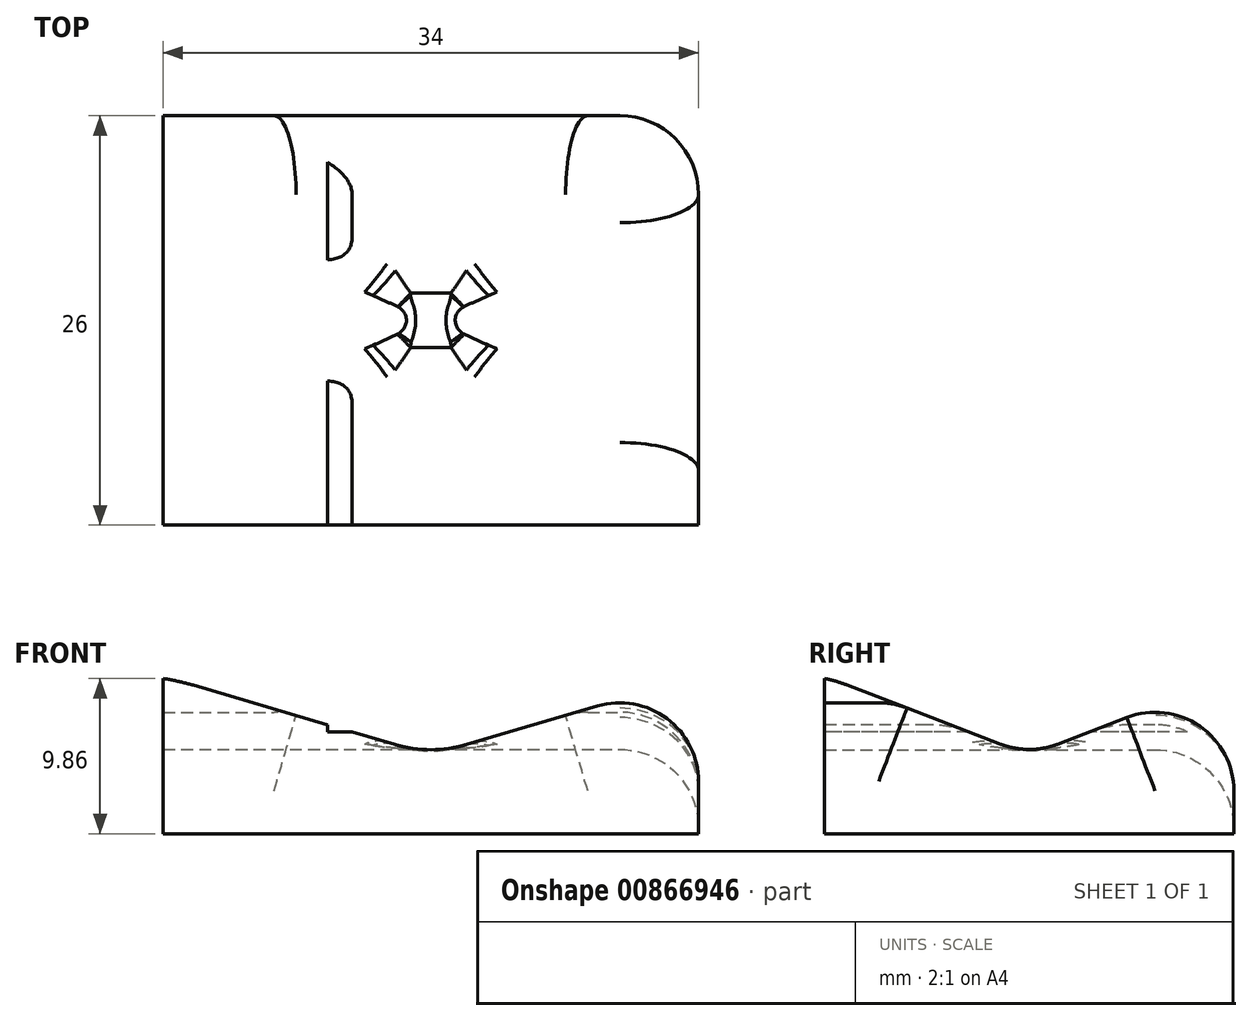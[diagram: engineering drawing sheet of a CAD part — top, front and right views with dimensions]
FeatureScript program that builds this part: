
annotation { "Feature Type Name" : "Feature", "Feature Type Description" : "" }
export const myFeature = defineFeature(function(context is Context, id is Id, definition is map)
    precondition{}
    {
        {
            var Q0;
            Q0=qCreatedBy(makeId("Top.planeOp"),FACE);
            var sketch = newSketch(context, id + "F0", { "sketchPlane" : qUnion([Q0])});
            skLineSegment(sketch, "E0.bottom", {"start": v(-17, -13) * mm, "end": v(17, -13) * mm});
            skLineSegment(sketch, "E0.top", {"start": v(-17, 13) * mm, "end": v(17, 13) * mm});
            skLineSegment(sketch, "E0.left", {"start": v(-17, -13) * mm, "end": v(-17, 13) * mm});
            skLineSegment(sketch, "E0.right", {"start": v(17, -13) * mm, "end": v(17, 13) * mm});
            skLineSegment(sketch, "E1", {"start": v(-17, 13) * mm, "end": v(17, -13) * mm, "construction": true});
            skSolve(sketch);
        }
        {
            var Q0;
            Q0 = qSketchRegion(id + "F0", true);
            extrude(context, id + "F1", {"entities" : qUnion([Q0]), "depth" : 10 * mm, "offsetDistance" : 25 * mm});
        }
        {
            var Q0;
            Q0=makeQuery(id+"F1.opExtrude","SWEPT_FACE",FACE,{"disambiguationData":[OSD([sQuery(id+"F0.wireOp",EDGE,"E0.left")])]});
            var sketch = newSketch(context, id + "F2", { "sketchPlane" : qUnion([Q0])});
            skLineSegment(sketch, "E2", {"start": v(-13, 10) * mm, "end": v(0, 5) * mm});
            skLineSegment(sketch, "E3", {"start": v(0, 5) * mm, "end": v(13, 10) * mm});
            skLineSegment(sketch, "E4", {"start": v(-13, 10) * mm, "end": v(13, 10) * mm});
            skSolve(sketch);
        }
        {
            var Q0;
            Q0 = qSketchRegion(id + "F2", true);
            extrude(context, id + "F3", {"entities" : qUnion([Q0]), "operationType" : NewBodyOperationType.REMOVE, "endBound" : BoundingType.THROUGH_ALL, "oppositeDirection" : true, "depth" : 25 * mm, "offsetDistance" : 25 * mm});
        }
        {
            var Q0;
            Q0=makeQuery(id+"F1.opExtrude","SWEPT_FACE",FACE,{"disambiguationData":[OSD([sQuery(id+"F0.wireOp",EDGE,"E0.bottom")])]});
            var sketch = newSketch(context, id + "F4", { "sketchPlane" : qUnion([Q0])});
            skLineSegment(sketch, "E5", {"start": v(-17, 10) * mm, "end": v(0, 5) * mm});
            skLineSegment(sketch, "E6", {"start": v(0, 5) * mm, "end": v(17, 10) * mm});
            skLineSegment(sketch, "E7", {"start": v(17, 10) * mm, "end": v(-17, 10) * mm});
            skSolve(sketch);
        }
        {
            var Q0;
            Q0 = qSketchRegion(id + "F4", true);
            extrude(context, id + "F5", {"entities" : qUnion([Q0]), "operationType" : NewBodyOperationType.REMOVE, "endBound" : BoundingType.THROUGH_ALL, "oppositeDirection" : true, "depth" : 25 * mm, "offsetDistance" : 25 * mm});
        }
        {
            var Q0;
            {var subQ0=sQuery(id+"F2.wireOp",EDGE,"E3");var subQ1=sQuery(id+"F2.wireOp",EDGE,"E2");Q0=makeQuery(id+"F5.boolean.opBoolean","SPLIT",EDGE,{"disambiguationData":[TD([makeQuery(id+"F1.opExtrude","SWEPT_FACE",FACE,{"disambiguationData":[OSD([sQuery(id+"F0.wireOp",EDGE,"E0.left")])]})])],"derivedFrom":makeQuery(id+"F3.boolean.opBoolean","COPY",EDGE,{"derivedFrom":makeQuery(id+"F3.opExtrude","SWEPT_EDGE",EDGE,{"disambiguationData":[OSD([subQ1,subQ0])]})})});}
            var Q1;
            {var subQ0=sQuery(id+"F2.wireOp",EDGE,"E3");var subQ1=sQuery(id+"F2.wireOp",EDGE,"E2");Q1=makeQuery(id+"F5.boolean.opBoolean","SPLIT",EDGE,{"disambiguationData":[TD([makeQuery(id+"F1.opExtrude","SWEPT_FACE",FACE,{"disambiguationData":[OSD([sQuery(id+"F0.wireOp",EDGE,"E0.right")])]})])],"derivedFrom":makeQuery(id+"F3.boolean.opBoolean","COPY",EDGE,{"derivedFrom":makeQuery(id+"F3.opExtrude","SWEPT_EDGE",EDGE,{"disambiguationData":[OSD([subQ1,subQ0])]})})});}
            fillet(context, id + "F6", {"entities" : qUnion([Q0, Q1]), "radius" : 5 * mm, "tangentPropagation" : true, "allowEdgeOverflow" : false});
        }
        {
            var Q0;
            {var subQ0=sQuery(id+"F4.wireOp",EDGE,"E5");var subQ1=sQuery(id+"F4.wireOp",EDGE,"E6");Q0=makeQuery(id+"F5.boolean.opBoolean","COPY",EDGE,{"disambiguationData":[TD([makeQuery(id+"F1.opExtrude","SWEPT_FACE",FACE,{"disambiguationData":[OSD([sQuery(id+"F0.wireOp",EDGE,"E0.top")])]})])],"derivedFrom":makeQuery(id+"F5.opExtrude","SWEPT_EDGE",EDGE,{"disambiguationData":[OSD([subQ0,subQ1])]})});}
            fillet(context, id + "F7", {"entities" : qUnion([Q0]), "radius" : 8 * mm, "tangentPropagation" : true, "allowEdgeOverflow" : false});
        }
        {
            var Q0;
            Q0=makeQuery(id+"F5.boolean.opBoolean","INTERSECT",EDGE,{"derivedFrom":[makeQuery(id+"F1.opExtrude","SWEPT_FACE",FACE,{"disambiguationData":[OSD([sQuery(id+"F0.wireOp",EDGE,"E0.top")])]}),makeQuery(id+"F5.opExtrude","SWEPT_FACE",FACE,{"disambiguationData":[OSD([sQuery(id+"F4.wireOp",EDGE,"E5")])]})]});
            var Q1;
            {var subQ0=makeQuery(id+"F1.opExtrude","SWEPT_FACE",FACE,{"disambiguationData":[OSD([sQuery(id+"F0.wireOp",EDGE,"E0.top")])]});var subQ1=sQuery(id+"F4.wireOp",EDGE,"E5");var subQ2=sQuery(id+"F4.wireOp",EDGE,"E6");Q1=makeQuery(id+"F7.opFillet","BLEND_EDGE",EDGE,{"blendedFrom":[makeQuery(id+"F5.boolean.opBoolean","COPY",EDGE,{"disambiguationData":[TD([subQ0])],"derivedFrom":makeQuery(id+"F5.opExtrude","SWEPT_EDGE",EDGE,{"disambiguationData":[OSD([subQ1,subQ2])]})}),subQ0],"blendedInto":[subQ0]});}
            var Q2;
            Q2=makeQuery(id+"F5.boolean.opBoolean","INTERSECT",EDGE,{"derivedFrom":[makeQuery(id+"F1.opExtrude","SWEPT_FACE",FACE,{"disambiguationData":[OSD([sQuery(id+"F0.wireOp",EDGE,"E0.top")])]}),makeQuery(id+"F5.opExtrude","SWEPT_FACE",FACE,{"disambiguationData":[OSD([sQuery(id+"F4.wireOp",EDGE,"E6")])]})]});
            var Q3;
            Q3=makeQuery(id+"F3.boolean.opBoolean","INTERSECT",EDGE,{"derivedFrom":[makeQuery(id+"F1.opExtrude","SWEPT_FACE",FACE,{"disambiguationData":[OSD([sQuery(id+"F0.wireOp",EDGE,"E0.right")])]}),makeQuery(id+"F3.opExtrude","SWEPT_FACE",FACE,{"disambiguationData":[OSD([sQuery(id+"F2.wireOp",EDGE,"E2")])]})]});
            var Q4;
            Q4=makeQuery(id+"F3.boolean.opBoolean","COPY",EDGE,{"derivedFrom":makeQuery(id+"F3.opExtrude","CAP_EDGE",EDGE,{"disambiguationData":[OSD([sQuery(id+"F2.wireOp",EDGE,"E2")])],"isStart":true})});
            var Q5;
            Q5=makeQuery(id+"F5.boolean.opBoolean","COPY",EDGE,{"derivedFrom":makeQuery(id+"F5.opExtrude","CAP_EDGE",EDGE,{"disambiguationData":[OSD([sQuery(id+"F4.wireOp",EDGE,"E5")])],"isStart":true})});
            var Q6;
            Q6=makeQuery(id+"F5.boolean.opBoolean","COPY",EDGE,{"derivedFrom":makeQuery(id+"F5.opExtrude","CAP_EDGE",EDGE,{"disambiguationData":[OSD([sQuery(id+"F4.wireOp",EDGE,"E6")])],"isStart":true})});
            fillet(context, id + "F8", {"entities" : qUnion([Q0, Q1, Q2, Q3, Q4, Q5, Q6]), "radius" : 5 * mm, "tangentPropagation" : true, "allowEdgeOverflow" : false});
        }
        {
            var Q0;
            Q0=makeQuery(id+"F5.boolean.opBoolean","INTERSECT",EDGE,{"derivedFrom":[makeQuery(id+"F3.boolean.opBoolean","COPY",FACE,{"derivedFrom":makeQuery(id+"F3.opExtrude","SWEPT_FACE",FACE,{"disambiguationData":[OSD([sQuery(id+"F2.wireOp",EDGE,"E2")])]})}),makeQuery(id+"F5.opExtrude","SWEPT_FACE",FACE,{"disambiguationData":[OSD([sQuery(id+"F4.wireOp",EDGE,"E5")])]})]});
            var Q1;
            Q1=makeQuery(id+"F5.boolean.opBoolean","INTERSECT",EDGE,{"derivedFrom":[makeQuery(id+"F3.boolean.opBoolean","COPY",FACE,{"derivedFrom":makeQuery(id+"F3.opExtrude","SWEPT_FACE",FACE,{"disambiguationData":[OSD([sQuery(id+"F2.wireOp",EDGE,"E3")])]})}),makeQuery(id+"F5.opExtrude","SWEPT_FACE",FACE,{"disambiguationData":[OSD([sQuery(id+"F4.wireOp",EDGE,"E5")])]})]});
            var Q2;
            Q2=makeQuery(id+"F8.opFillet","BLEND_EDGE",EDGE,{"blendedFrom":[makeQuery(id+"F3.boolean.opBoolean","COPY",EDGE,{"derivedFrom":makeQuery(id+"F3.opExtrude","CAP_EDGE",EDGE,{"disambiguationData":[OSD([sQuery(id+"F2.wireOp",EDGE,"E3")])],"isStart":true})}),makeQuery(id+"F5.boolean.opBoolean","COPY",EDGE,{"derivedFrom":makeQuery(id+"F5.opExtrude","CAP_EDGE",EDGE,{"disambiguationData":[OSD([sQuery(id+"F4.wireOp",EDGE,"E5")])],"isStart":true})})],"blendedInto":[]});
            var Q3;
            Q3=makeQuery(id+"F8.opFillet","BLEND_EDGE",EDGE,{"blendedFrom":[makeQuery(id+"F3.boolean.opBoolean","INTERSECT",EDGE,{"derivedFrom":[makeQuery(id+"F1.opExtrude","SWEPT_FACE",FACE,{"disambiguationData":[OSD([sQuery(id+"F0.wireOp",EDGE,"E0.right")])]}),makeQuery(id+"F3.opExtrude","SWEPT_FACE",FACE,{"disambiguationData":[OSD([sQuery(id+"F2.wireOp",EDGE,"E3")])]})]}),makeQuery(id+"F5.boolean.opBoolean","COPY",EDGE,{"derivedFrom":makeQuery(id+"F5.opExtrude","CAP_EDGE",EDGE,{"disambiguationData":[OSD([sQuery(id+"F4.wireOp",EDGE,"E6")])],"isStart":true})})],"blendedInto":[]});
            var Q4;
            Q4=makeQuery(id+"F8.opFillet","BLEND_EDGE",EDGE,{"blendedFrom":[makeQuery(id+"F3.boolean.opBoolean","INTERSECT",EDGE,{"derivedFrom":[makeQuery(id+"F1.opExtrude","SWEPT_FACE",FACE,{"disambiguationData":[OSD([sQuery(id+"F0.wireOp",EDGE,"E0.right")])]}),makeQuery(id+"F3.opExtrude","SWEPT_FACE",FACE,{"disambiguationData":[OSD([sQuery(id+"F2.wireOp",EDGE,"E2")])]})]}),makeQuery(id+"F5.boolean.opBoolean","INTERSECT",EDGE,{"derivedFrom":[makeQuery(id+"F1.opExtrude","SWEPT_FACE",FACE,{"disambiguationData":[OSD([sQuery(id+"F0.wireOp",EDGE,"E0.top")])]}),makeQuery(id+"F5.opExtrude","SWEPT_FACE",FACE,{"disambiguationData":[OSD([sQuery(id+"F4.wireOp",EDGE,"E6")])]})]})],"blendedInto":[]});
            var Q5;
            Q5=makeQuery(id+"F5.boolean.opBoolean","INTERSECT",EDGE,{"derivedFrom":[makeQuery(id+"F3.boolean.opBoolean","COPY",FACE,{"derivedFrom":makeQuery(id+"F3.opExtrude","SWEPT_FACE",FACE,{"disambiguationData":[OSD([sQuery(id+"F2.wireOp",EDGE,"E2")])]})}),makeQuery(id+"F5.opExtrude","SWEPT_FACE",FACE,{"disambiguationData":[OSD([sQuery(id+"F4.wireOp",EDGE,"E6")])]})]});
            fillet(context, id + "F9", {"entities" : qUnion([Q0, Q1, Q2, Q3, Q4, Q5]), "radius" : 5 * mm, "tangentPropagation" : true, "allowEdgeOverflow" : false});
        }
        {
            var Q0;
            Q0=makeQuery(id+"F1.opExtrude","SWEPT_FACE",FACE,{"disambiguationData":[OSD([sQuery(id+"F0.wireOp",EDGE,"E0.bottom")])]});
            var sketch = newSketch(context, id + "F10", { "sketchPlane" : qUnion([Q0])});
            skLineSegment(sketch, "E8.bottom", {"start": v(-6.56, 6.47) * mm, "end": v(-0.26, 6.47) * mm});
            skLineSegment(sketch, "E8.top", {"start": v(-6.56, 15.46) * mm, "end": v(-0.26, 15.46) * mm});
            skLineSegment(sketch, "E8.left", {"start": v(-6.56, 6.47) * mm, "end": v(-6.56, 15.46) * mm});
            skLineSegment(sketch, "E8.right", {"start": v(-0.26, 6.47) * mm, "end": v(-0.26, 15.46) * mm});
            skSolve(sketch);
        }
        {
            var Q0;
            Q0 = qSketchRegion(id + "F10", true);
            extrude(context, id + "F11", {"entities" : qUnion([Q0]), "operationType" : NewBodyOperationType.REMOVE, "endBound" : BoundingType.THROUGH_ALL, "oppositeDirection" : true, "depth" : 25 * mm, "offsetDistance" : 25 * mm});
        }
    });
